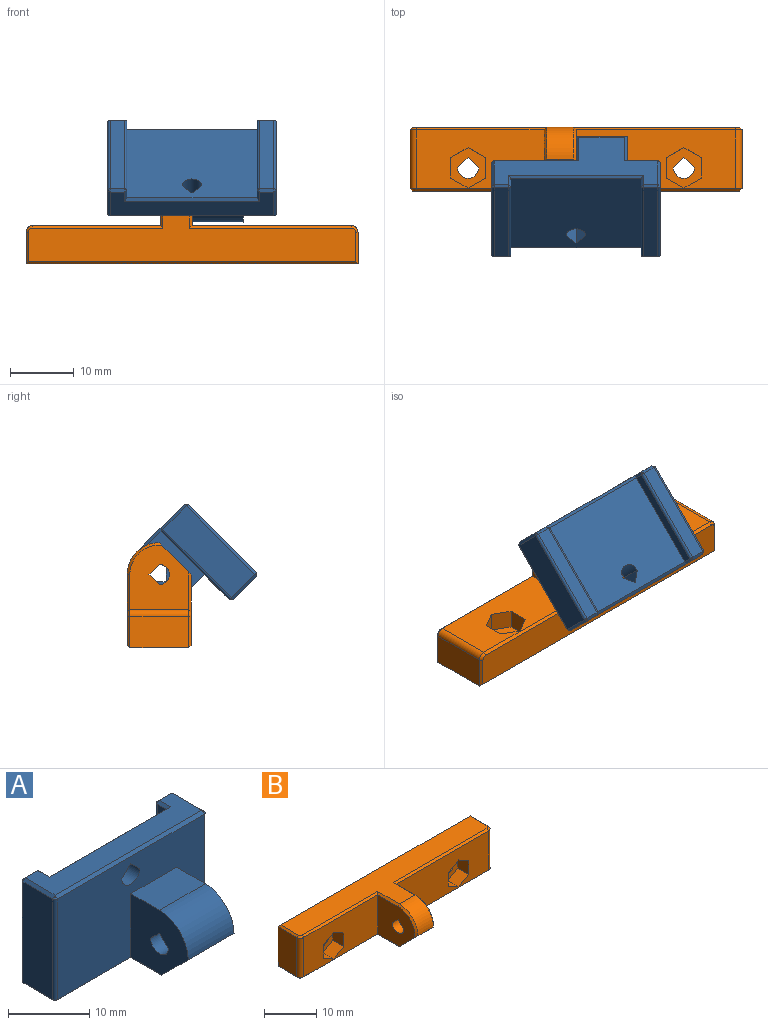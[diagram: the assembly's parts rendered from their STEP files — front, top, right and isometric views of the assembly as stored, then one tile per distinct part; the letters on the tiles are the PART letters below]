
ASSEMBLY  parts=2 mates=1
PART A: 66 faces, bbox 26.4x16x16 mm
  f0: plane 25.6x15.2mm, normal (0,-1,0), area 306.1mm2, adj f13,f16,f17,f25,f26,f27,f28,f33
  f1: plane 20.4x15.2mm, normal (0,1,0), area 303.9mm2, adj f7,f8,f25,f26,f27,f38,f56
  f2: cylinder r=1.55mm len=5mm, axis (-1,0,0), area 24.3mm2, adj f3,f4,f17,f24
  f3: plane 5x1.55mm, normal (0,0.71,-0.71), area 11mm2, adj f2,f4,f17,f24
  f4: plane 5x1.55mm, normal (0,-0.71,-0.71), area 11mm2, adj f2,f3,f17,f24
  f5: plane 15.2x5.2mm, normal (1,0,0), area 79mm2, adj f28,f29,f39,f65
  f6: plane 15.2x2.2mm, normal (0,1,0), area 33.4mm2, adj f29,f30,f35,f62
  f7: plane 15.2x1.6mm, normal (-1,0,0), area 24.3mm2, adj f1,f30,f36,f58
  f8: plane 15.2x1.6mm, normal (1,0,0), area 24.3mm2, adj f1,f31,f40,f54
  f9: plane 15.2x2.2mm, normal (0,1,0), area 33.4mm2, adj f31,f32,f44,f53
  f10: plane 15.2x5.2mm, normal (-1,0,0), area 79mm2, adj f32,f33,f48,f57
  f11: plane 25.6x5.2mm, normal (0,0,1), area 90.7mm2, adj f53,f54,f56,f57,f58,f61,f62,f65
  f12: plane 25.6x10.43mm, normal (0,0,-1), area 128.4mm2, adj f35,f36,f38,f39,f40,f43,f44,f45
  f13: plane 8x5mm, normal (0,0,1), area 40mm2, adj f0,f14,f16,f17
  f14: cylinder r=5mm len=8mm, axis (-1,0,0), area 62.8mm2, adj f13,f15,f16,f17
  f15: plane 8x4.88mm, normal (0,-0.71,-0.71), area 55.1mm2, adj f14,f16,f17,f45,f47,f49
  f16: plane 10x9.6mm, normal (1,0,0), area 52.9mm2, adj f0,f13,f14,f15,f18,f19,f20,f21
  f17: plane 10x9.6mm, normal (-1,0,0), area 73.9mm2, adj f0,f2,f3,f4,f13,f14,f15,f49
  f18: plane 3.23x3mm, normal (0,-1,0), area 9.7mm2, adj f16,f19,f23,f24
  f19: plane 3x2.8mm, normal (0,-0.5,-0.87), area 9.7mm2, adj f16,f18,f20,f24
  f20: plane 3x2.8mm, normal (0,0.5,-0.87), area 9.7mm2, adj f16,f19,f21,f24
  f21: plane 3.23x3mm, normal (0,1,0), area 9.7mm2, adj f16,f20,f22,f24
  f22: plane 3x2.8mm, normal (0,0.5,0.87), area 9.7mm2, adj f16,f21,f23,f24
  f23: plane 3x2.8mm, normal (0,-0.5,0.87), area 9.7mm2, adj f16,f18,f22,f24
  f24: plane 6.47x5.6mm, normal (1,0,0), area 21mm2, adj f2,f3,f4,f18,f19,f20,f21,f22
  f25: plane 4x1.55mm, normal (0.71,0,-0.71), area 8.8mm2, adj f0,f1,f26,f27
  f26: cylinder r=1.55mm len=4mm, axis (0,-1,0), area 19.5mm2, adj f0,f1,f25,f27
  f27: plane 4x1.55mm, normal (-0.71,0,-0.71), area 8.8mm2, adj f0,f1,f25,f26
  f28: cylinder r=0.4mm len=15.2mm, axis (0,0,1), area 9.6mm2, adj f0,f5,f41,f63
  f29: cylinder r=0.4mm len=15.2mm, axis (0,0,-1), area 9.6mm2, adj f5,f6,f37,f64
  f30: cylinder r=0.4mm len=15.2mm, axis (0,0,-1), area 9.6mm2, adj f6,f7,f34,f60
  f31: cylinder r=0.4mm len=15.2mm, axis (0,0,-1), area 9.6mm2, adj f8,f9,f42,f52
  f32: cylinder r=0.4mm len=15.2mm, axis (0,0,-1), area 9.6mm2, adj f9,f10,f46,f55
  f33: cylinder r=0.4mm len=15.2mm, axis (0,0,-1), area 9.6mm2, adj f0,f10,f50,f59
  f34: cone r=0.4mm half-angle=45deg, axis (0,0,1), area 0.2mm2, adj f30,f35,f36
  f35: plane 2.2x0.4mm, normal (0,0.71,-0.71), area 1.2mm2, adj f6,f12,f34,f37
  f36: plane 2x0.4mm, normal (-0.71,0,-0.71), area 1mm2, adj f7,f12,f34,f38
  f37: cone r=0.4mm half-angle=45deg, axis (0,0,1), area 0.2mm2, adj f29,f35,f39
  f38: plane 21.2x0.4mm, normal (0,0.71,-0.71), area 11.8mm2, adj f1,f12,f36,f40
  f39: plane 5.2x0.4mm, normal (0.71,0,-0.71), area 2.9mm2, adj f5,f12,f37,f41
  f40: plane 2x0.4mm, normal (0.71,0,-0.71), area 1mm2, adj f8,f12,f38,f42
  f41: cone r=0.4mm half-angle=45deg, axis (0,0,1), area 0.2mm2, adj f28,f39,f43
  f42: cone r=0.4mm half-angle=45deg, axis (0,0,1), area 0.2mm2, adj f31,f40,f44
  f43: plane 5.2x0.4mm, normal (0,-0.71,-0.71), area 2.8mm2, adj f0,f12,f41,f45
  f44: plane 2.2x0.4mm, normal (0,0.71,-0.71), area 1.2mm2, adj f9,f12,f42,f46
  f45: plane 5.8x0.4mm, normal (0.71,0,-0.71), area 3mm2, adj f12,f15,f16,f43,f47
  f46: cone r=0.4mm half-angle=45deg, axis (0,0,1), area 0.2mm2, adj f32,f44,f48
  f47: plane 7.43x0.28mm, normal (0,-0.38,-0.92), area 2.2mm2, adj f12,f15,f45,f49
  f48: plane 5.2x0.4mm, normal (-0.71,0,-0.71), area 2.9mm2, adj f10,f12,f46,f50
  f49: plane 5.8x0.4mm, normal (-0.71,0,-0.71), area 3mm2, adj f12,f15,f17,f47,f51
  f50: cone r=0.4mm half-angle=45deg, axis (0,0,1), area 0.2mm2, adj f33,f48,f51
  f51: plane 13.2x0.4mm, normal (0,-0.71,-0.71), area 7.4mm2, adj f0,f12,f49,f50
  f52: cone r=0.4mm half-angle=45deg, axis (0,0,-1), area 0.2mm2, adj f31,f53,f54
  f53: plane 2.2x0.4mm, normal (0,0.71,0.71), area 1.2mm2, adj f9,f11,f52,f55
  f54: plane 2x0.4mm, normal (0.71,0,0.71), area 1mm2, adj f8,f11,f52,f56
  f55: cone r=0.4mm half-angle=45deg, axis (0,0,-1), area 0.2mm2, adj f32,f53,f57
  f56: plane 21.2x0.4mm, normal (0,0.71,0.71), area 11.8mm2, adj f1,f11,f54,f58
  f57: plane 5.2x0.4mm, normal (-0.71,0,0.71), area 2.9mm2, adj f10,f11,f55,f59
  f58: plane 2x0.4mm, normal (-0.71,0,0.71), area 1mm2, adj f7,f11,f56,f60
  f59: cone r=0.4mm half-angle=45deg, axis (0,0,-1), area 0.2mm2, adj f33,f57,f61
  f60: cone r=0.4mm half-angle=45deg, axis (0,0,-1), area 0.2mm2, adj f30,f58,f62
  f61: plane 25.6x0.4mm, normal (0,-0.71,0.71), area 14.5mm2, adj f0,f11,f59,f63
  f62: plane 2.2x0.4mm, normal (0,0.71,0.71), area 1.2mm2, adj f6,f11,f60,f64
  f63: cone r=0.4mm half-angle=45deg, axis (0,0,-1), area 0.2mm2, adj f28,f61,f65
  f64: cone r=0.4mm half-angle=45deg, axis (0,0,-1), area 0.2mm2, adj f29,f62,f65
  f65: plane 5.2x0.4mm, normal (0.71,0,0.71), area 2.9mm2, adj f5,f11,f63,f64
PART B: 57 faces, bbox 52x16.5x10 mm
  f0: plane 25x9.2mm, normal (0,-1,0), area 203.8mm2, adj f13,f14,f15,f16,f17,f18,f33,f35
  f1: cylinder r=1.65mm len=3.3mm, axis (0,1,0), area 15.6mm2, adj f2,f5,f12,f26
  f2: plane 3x1.65mm, normal (0.71,0,-0.71), area 7mm2, adj f1,f5,f12,f26
  f3: cylinder r=1.65mm len=3.3mm, axis (0,1,0), area 15.6mm2, adj f4,f6,f12,f19
  f4: plane 3x1.65mm, normal (0.71,0,-0.71), area 7mm2, adj f3,f6,f12,f19
  f5: plane 3x1.65mm, normal (-0.71,0,-0.71), area 7mm2, adj f1,f2,f12,f26
  f6: plane 3x1.65mm, normal (-0.71,0,-0.71), area 7mm2, adj f3,f4,f12,f19
  f7: plane 51.2x11.1mm, normal (0,0,1), area 290.9mm2, adj f29,f37,f38,f39,f40,f41,f42,f43
  f8: plane 9.2x5mm, normal (-1,0,0), area 46mm2, adj f12,f34,f42,f49
  f9: plane 51.2x10.93mm, normal (0,0,-1), area 290.2mm2, adj f47,f48,f49,f50,f51,f52,f53,f54
  f10: plane 9.2x5mm, normal (1,0,0), area 46mm2, adj f12,f35,f40,f53
  f11: plane 20x9.2mm, normal (0,-1,0), area 157.8mm2, adj f20,f21,f22,f23,f24,f25,f32,f34
  f12: plane 52x9.2mm, normal (0,1,0), area 464.4mm2, adj f1,f2,f3,f4,f5,f6,f8,f10
  f13: plane 3x2.75mm, normal (-0.5,0,-0.87), area 9.5mm2, adj f0,f14,f18,f19
  f14: plane 3x2.75mm, normal (0.5,0,-0.87), area 9.5mm2, adj f0,f13,f15,f19
  f15: plane 3.18x3mm, normal (1,0,0), area 9.5mm2, adj f0,f14,f16,f19
  f16: plane 3x2.75mm, normal (0.5,0,0.87), area 9.5mm2, adj f0,f15,f17,f19
  f17: plane 3x2.75mm, normal (-0.5,0,0.87), area 9.5mm2, adj f0,f16,f18,f19
  f18: plane 3.18x3mm, normal (-1,0,0), area 9.5mm2, adj f0,f13,f17,f19
  f19: plane 6.35x5.5mm, normal (0,-1,0), area 19.2mm2, adj f3,f4,f6,f13,f14,f15,f16,f17
  f20: plane 3.18x3mm, normal (-1,0,0), area 9.5mm2, adj f11,f21,f25,f26
  f21: plane 3x2.75mm, normal (-0.5,0,-0.87), area 9.5mm2, adj f11,f20,f22,f26
  f22: plane 3x2.75mm, normal (0.5,0,-0.87), area 9.5mm2, adj f11,f21,f23,f26
  f23: plane 3.18x3mm, normal (1,0,0), area 9.5mm2, adj f11,f22,f24,f26
  f24: plane 3x2.75mm, normal (0.5,0,0.87), area 9.5mm2, adj f11,f23,f25,f26
  f25: plane 3x2.75mm, normal (-0.5,0,0.87), area 9.5mm2, adj f11,f20,f24,f26
  f26: plane 6.35x5.5mm, normal (0,-1,0), area 19.2mm2, adj f1,f2,f5,f20,f21,f22,f23,f24
  f27: cylinder r=1.6mm len=5mm, axis (1,0,0), area 25.1mm2, adj f28,f31,f32,f33
  f28: plane 5x1.6mm, normal (0,0.71,-0.71), area 11.3mm2, adj f27,f31,f32,f33
  f29: cylinder r=5mm len=5mm, axis (1,0,0), area 33mm2, adj f7,f30,f36,f46
  f30: plane 5x4.88mm, normal (0,-0.71,-0.71), area 34.2mm2, adj f29,f32,f33,f36,f46,f50,f52,f54
  f31: plane 5x1.6mm, normal (0,-0.71,-0.71), area 11.3mm2, adj f27,f28,f32,f33
  f32: plane 10.1x9.2mm, normal (-1,0,0), area 73mm2, adj f11,f27,f28,f30,f31,f45,f46,f50
  f33: plane 10.1x9.2mm, normal (1,0,0), area 73mm2, adj f0,f27,f28,f30,f31,f36,f37,f54
  f34: cylinder r=1mm len=9.2mm, axis (0,0,1), area 14.5mm2, adj f8,f11,f43,f47
  f35: cylinder r=1mm len=9.2mm, axis (0,0,-1), area 14.5mm2, adj f0,f10,f39,f55
  f36: cone r=4.6mm half-angle=45deg, axis (-1,0,0), area 4.4mm2, adj f29,f30,f33,f37
  f37: plane 5.9x0.4mm, normal (0.71,0,0.71), area 3.2mm2, adj f7,f33,f36,f38
  f38: plane 25.4x0.4mm, normal (0,-0.71,0.71), area 14.3mm2, adj f0,f7,f37,f39
  f39: cone r=0.6mm half-angle=45deg, axis (0,0,-1), area 0.7mm2, adj f7,f35,f38,f40
  f40: plane 5x0.4mm, normal (0.71,0,0.71), area 2.7mm2, adj f7,f10,f39,f41
  f41: plane 52x0.4mm, normal (0,0.71,0.71), area 29.2mm2, adj f7,f12,f40,f42
  f42: plane 5x0.4mm, normal (-0.71,0,0.71), area 2.7mm2, adj f7,f8,f41,f43
  f43: cone r=0.6mm half-angle=45deg, axis (0,0,-1), area 0.7mm2, adj f7,f34,f42,f44
  f44: plane 20.4x0.4mm, normal (0,-0.71,0.71), area 11.4mm2, adj f7,f11,f43,f45
  f45: plane 5.9x0.4mm, normal (-0.71,0,0.71), area 3.2mm2, adj f7,f32,f44,f46
  f46: cone r=5mm half-angle=45deg, axis (1,0,0), area 4.4mm2, adj f29,f30,f32,f45
  f47: cone r=0.6mm half-angle=45deg, axis (0,0,1), area 0.7mm2, adj f9,f34,f48,f49
  f48: plane 20.4x0.4mm, normal (0,-0.71,-0.71), area 11.4mm2, adj f9,f11,f47,f50
  f49: plane 5x0.4mm, normal (-0.71,0,-0.71), area 2.7mm2, adj f8,f9,f47,f51
  f50: plane 6.3x0.4mm, normal (-0.71,0,-0.71), area 3.3mm2, adj f9,f30,f32,f48,f52
  f51: plane 52x0.4mm, normal (0,0.71,-0.71), area 29.2mm2, adj f9,f12,f49,f53
  f52: plane 4.43x0.28mm, normal (0,-0.38,-0.92), area 1.3mm2, adj f9,f30,f50,f54
  f53: plane 5x0.4mm, normal (0.71,0,-0.71), area 2.7mm2, adj f9,f10,f51,f55
  f54: plane 6.3x0.4mm, normal (0.71,0,-0.71), area 3.3mm2, adj f9,f30,f33,f52,f56
  f55: cone r=0.6mm half-angle=45deg, axis (0,0,1), area 0.7mm2, adj f9,f35,f53,f56
  f56: plane 25.4x0.4mm, normal (0,-0.71,-0.71), area 14.3mm2, adj f0,f9,f54,f55
PLACE A rot(axis=(1,0,0),135deg) t=(-30.07,-12.59,13.61)mm
PLACE B rot(axis=(-1,0,0),90deg) t=(-30.07,-17.59,-4.96)mm
MATE revolute A.f2 <-> B.f27  axis (-1,0,0) through (-30.07,-12.59,6.54)mm
